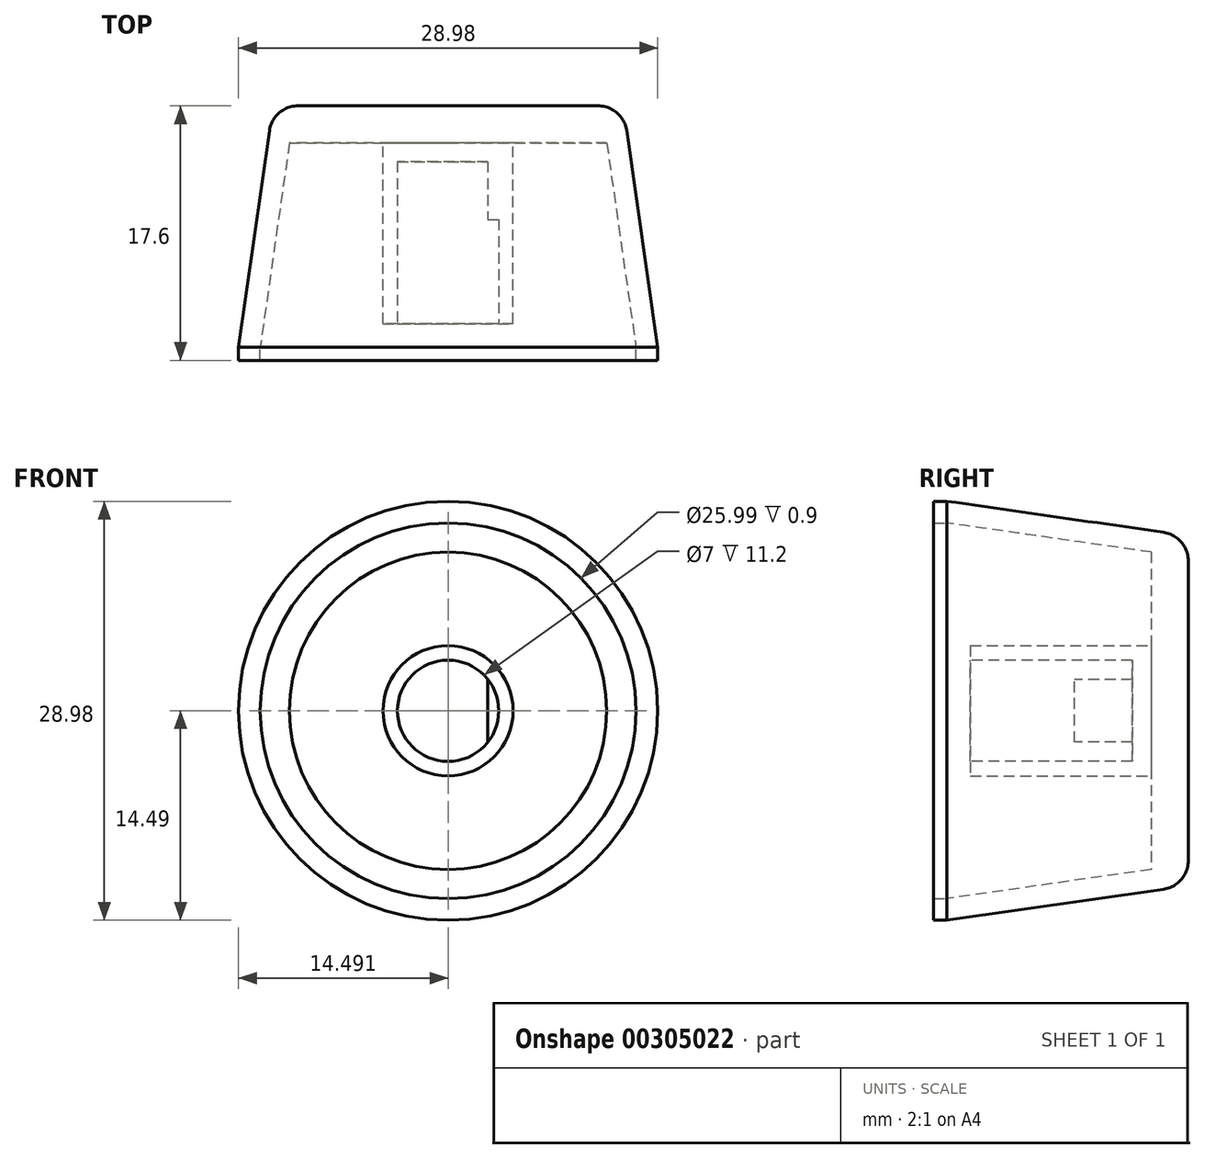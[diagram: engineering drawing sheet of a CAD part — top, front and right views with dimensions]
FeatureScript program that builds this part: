
annotation { "Feature Type Name" : "Feature", "Feature Type Description" : "" }
export const myFeature = defineFeature(function(context is Context, id is Id, definition is map)
    precondition{}
    {
        {
            var Q0;
            Q0=qCreatedBy(makeId("Top.planeOp"),FACE);
            var sketch = newSketch(context, id + "F0", { "sketchPlane" : qUnion([Q0])});
            skLineSegment(sketch, "E0", {"start": v(15.15, 0) * mm, "end": v(12.75, 16.7) * mm});
            skLineSegment(sketch, "E1", {"start": v(12.75, 16.7) * mm, "end": v(-11.47, 16.7) * mm});
            skLineSegment(sketch, "E2", {"start": v(-11.47, 16.7) * mm, "end": v(-13.85, 0) * mm});
            skLineSegment(sketch, "E3", {"start": v(-13.85, 0) * mm, "end": v(-12.35, 0) * mm});
            skLineSegment(sketch, "E4", {"start": v(-12.35, 0) * mm, "end": v(-10.33, 14.14) * mm});
            skLineSegment(sketch, "E5", {"start": v(-10.33, 14.14) * mm, "end": v(-3.86, 14.14) * mm});
            skLineSegment(sketch, "E6", {"start": v(-3.86, 14.14) * mm, "end": v(-3.86, 2.84) * mm});
            skLineSegment(sketch, "E7", {"start": v(-3.86, 2.84) * mm, "end": v(5.14, 2.84) * mm});
            skLineSegment(sketch, "E8", {"start": v(5.14, 2.84) * mm, "end": v(5.14, 14.14) * mm});
            skLineSegment(sketch, "E9", {"start": v(5.14, 14.14) * mm, "end": v(11.62, 14.14) * mm});
            skLineSegment(sketch, "E10", {"start": v(11.62, 14.14) * mm, "end": v(13.65, 0) * mm});
            skLineSegment(sketch, "E11", {"start": v(13.65, 0) * mm, "end": v(15.15, 0) * mm});
            skPoint(sketch, "E12", {"position": v(0.64, 16.7) * mm});
            skPoint(sketch, "E13", {"position": v(-11.47, 16.7) * mm});
            skPoint(sketch, "E14", {"position": v(12.75, 16.7) * mm});
            skLineSegment(sketch, "E15", {"start": v(0.64, 16.7) * mm, "end": v(0.64, -10.32) * mm});
            skSolve(sketch);
        }
        {
            var Q0;
            {var subQ0=sQuery(id+"F0.wireOp",EDGE,"E2");Q0=makeQuery(id+"F0.imprint","IMPRINT",FACE,{"disambiguationData":[TD([[makeQuery(id+"F0.imprint","IMPRINT",EDGE,{"derivedFrom":subQ0}),1.0]])]});}
            var Q1;
            Q1=sQuery(id+"F0.wireOp",EDGE,"E15");
            revolve(context, id + "F1", {"entities" : qUnion([Q0]), "axis" : qUnion([Q1]), "revolveType" : RevolveType.FULL});
        }
        {
            var Q0;
            Q0=makeQuery(id+"F1.opRevolve","SWEPT_EDGE",EDGE,{"disambiguationData":[OSD([sQuery(id+"F0.wireOp",EDGE,"E1"),sQuery(id+"F0.wireOp",EDGE,"E2")])]});
            fillet(context, id + "F2", {"entities" : qUnion([Q0]), "radius" : 2 * mm, "tangentPropagation" : true, "allowEdgeOverflow" : false});
        }
        {
            var Q0;
            Q0=makeQuery(id+"F1.opRevolve","SWEPT_FACE",FACE,{"disambiguationData":[OSD([sQuery(id+"F0.wireOp",EDGE,"E7")])]});
            var sketch = newSketch(context, id + "F3", { "sketchPlane" : qUnion([Q0])});
            skCircle(sketch, "E16", {"center": v(0.64, 0) * mm, "radius": 3.5 * mm});
            skLineSegment(sketch, "E17", {"start": v(3.4, -2.16) * mm, "end": v(3.4, 2.16) * mm});
            skSolve(sketch);
        }
        {
            var Q0;
            {var subQ0=sQuery(id+"F3.wireOp",EDGE,"E17");Q0=makeQuery(id+"F3.imprint","IMPRINT",FACE,{"disambiguationData":[TD([[makeQuery(id+"F3.imprint","IMPRINT",EDGE,{"derivedFrom":subQ0}),-1.0]])]});}
            var Q1;
            {var subQ0=sQuery(id+"F3.wireOp",EDGE,"E17");Q1=makeQuery(id+"F3.imprint","IMPRINT",FACE,{"disambiguationData":[TD([[makeQuery(id+"F3.imprint","IMPRINT",EDGE,{"derivedFrom":subQ0}),1.0]])]});}
            extrude(context, id + "F4", {"entities" : qUnion([Q0, Q1]), "operationType" : NewBodyOperationType.REMOVE, "oppositeDirection" : true, "depth" : 6 * mm});
        }
        {
            var Q0;
            {var subQ0=sQuery(id+"F3.wireOp",EDGE,"E17");Q0=makeQuery(id+"F3.imprint","IMPRINT",FACE,{"disambiguationData":[TD([[makeQuery(id+"F3.imprint","IMPRINT",EDGE,{"derivedFrom":subQ0}),1.0]])]});}
            extrude(context, id + "F5", {"entities" : qUnion([Q0]), "operationType" : NewBodyOperationType.REMOVE, "oppositeDirection" : true, "depth" : 10 * mm});
        }
        {
            var Q0;
            Q0=makeQuery(id+"F1.opRevolve","SWEPT_FACE",FACE,{"disambiguationData":[OSD([sQuery(id+"F0.wireOp",EDGE,"E3")])]});
            extrude(context, id + "F6", {"entities" : qUnion([Q0]), "operationType" : NewBodyOperationType.ADD, "depth" : 0.9 * mm});
        }
        {
            var Q0;
            Q0=makeQuery(id+"F3.imprint","IMPRINT",FACE,{"disambiguationData":[TD([[makeQuery(id+"F3.imprint","IMPRINT",EDGE,{"derivedFrom":makeQuery(id+"F1.opRevolve","SWEPT_EDGE",EDGE,{"disambiguationData":[OSD([sQuery(id+"F0.wireOp",EDGE,"E6"),sQuery(id+"F0.wireOp",EDGE,"E7")])]})}),-1.0]])]});
            extrude(context, id + "F7", {"entities" : qUnion([Q0]), "operationType" : NewBodyOperationType.ADD, "depth" : 1.2 * mm});
        }
    });
